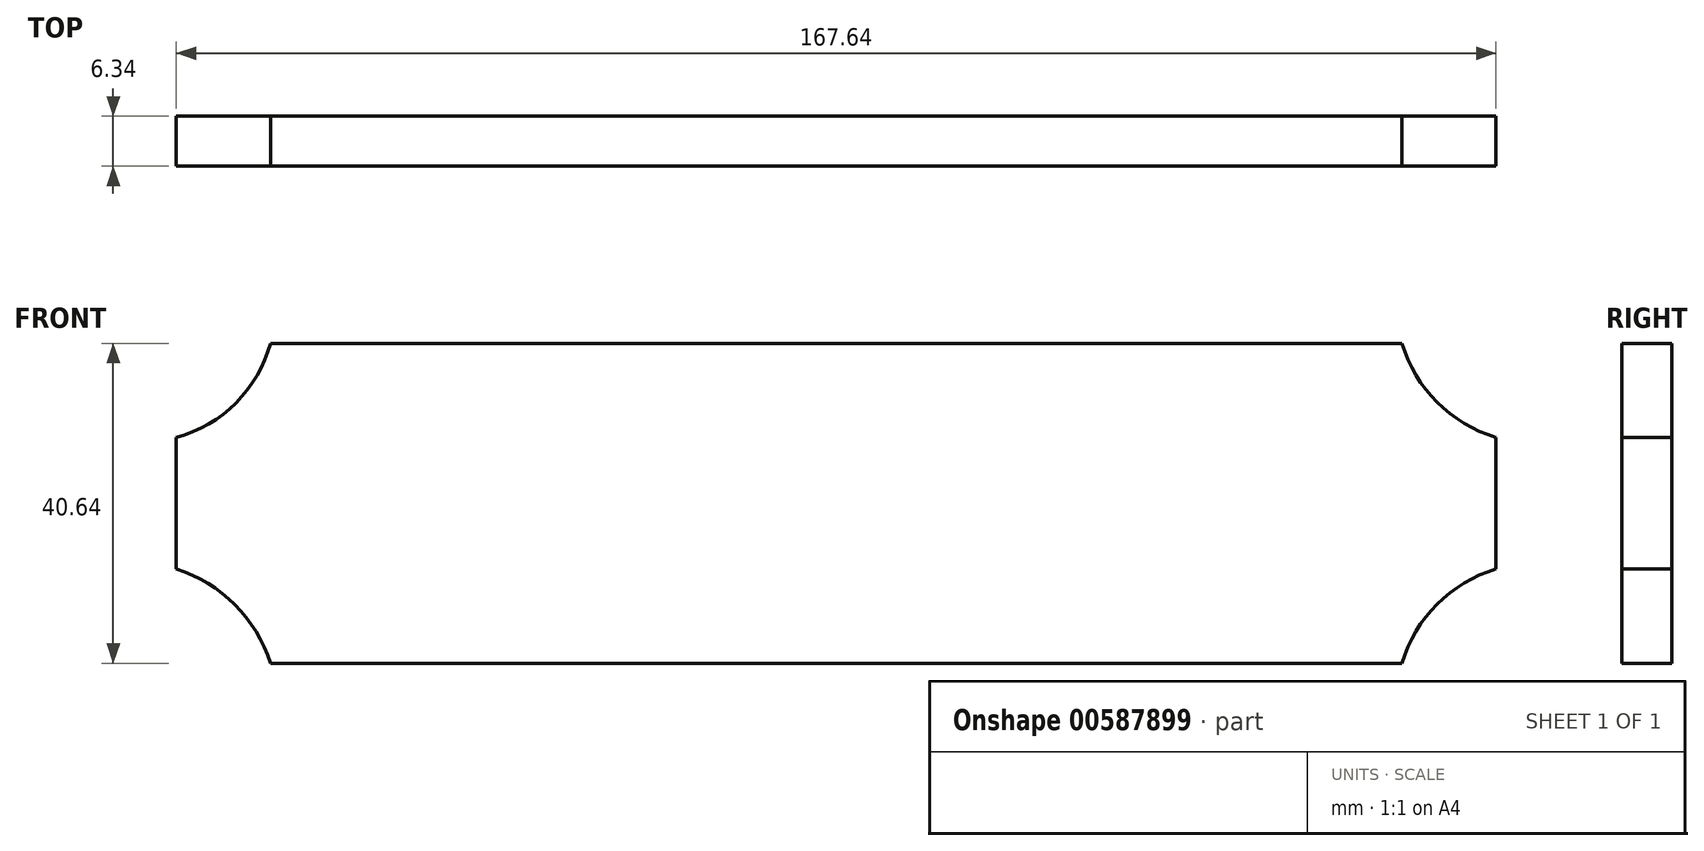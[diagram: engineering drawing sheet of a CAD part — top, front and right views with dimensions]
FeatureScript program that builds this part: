
annotation { "Feature Type Name" : "Feature", "Feature Type Description" : "" }
export const myFeature = defineFeature(function(context is Context, id is Id, definition is map)
    precondition{}
    {
        {
            var Q0;
            Q0=qCreatedBy(makeId("Front.planeOp"),FACE);
            var sketch = newSketch(context, id + "F0", { "sketchPlane" : qUnion([Q0])});
            skLineSegment(sketch, "E0", {"start": v(-71.87, 20.33) * mm, "end": v(71.86, 20.33) * mm});
            skLineSegment(sketch, "E1", {"start": v(-71.87, -20.3) * mm, "end": v(71.86, -20.3) * mm});
            skLineSegment(sketch, "E2", {"start": v(-83.82, 8.37) * mm, "end": v(-83.82, -8.35) * mm});
            skLineSegment(sketch, "E3", {"start": v(83.82, 8.37) * mm, "end": v(83.82, -8.35) * mm});
            skArc(sketch, "E4", {"start": v(-83.82, 8.37) * mm, "mid": v(-76.24, 12.75) * mm, "end": v(-71.87, 20.33) * mm});
            skArc(sketch, "E5", {"start": v(-71.87, -20.3) * mm, "mid": v(-76.39, -12.87) * mm, "end": v(-83.82, -8.35) * mm});
            skArc(sketch, "E6", {"start": v(71.86, 20.33) * mm, "mid": v(76.34, 12.85) * mm, "end": v(83.82, 8.37) * mm});
            skArc(sketch, "E7", {"start": v(83.82, -8.35) * mm, "mid": v(76.33, -12.83) * mm, "end": v(71.86, -20.3) * mm});
            skSolve(sketch);
        }
        {
            var Q0;
            Q0=makeQuery(id+"F0.imprint","IMPRINT",FACE,{"disambiguationData":[TD([[makeQuery(id+"F0.imprint","IMPRINT",EDGE,{"derivedFrom":sQuery(id+"F0.wireOp",EDGE,"E0")}),-1.0]])]});
            extrude(context, id + "F1", {"entities" : qUnion([Q0]), "endBound" : BoundingType.SYMMETRIC, "depth" : 6.35 * mm, "offsetDistance" : 25.4 * mm});
        }
    });
